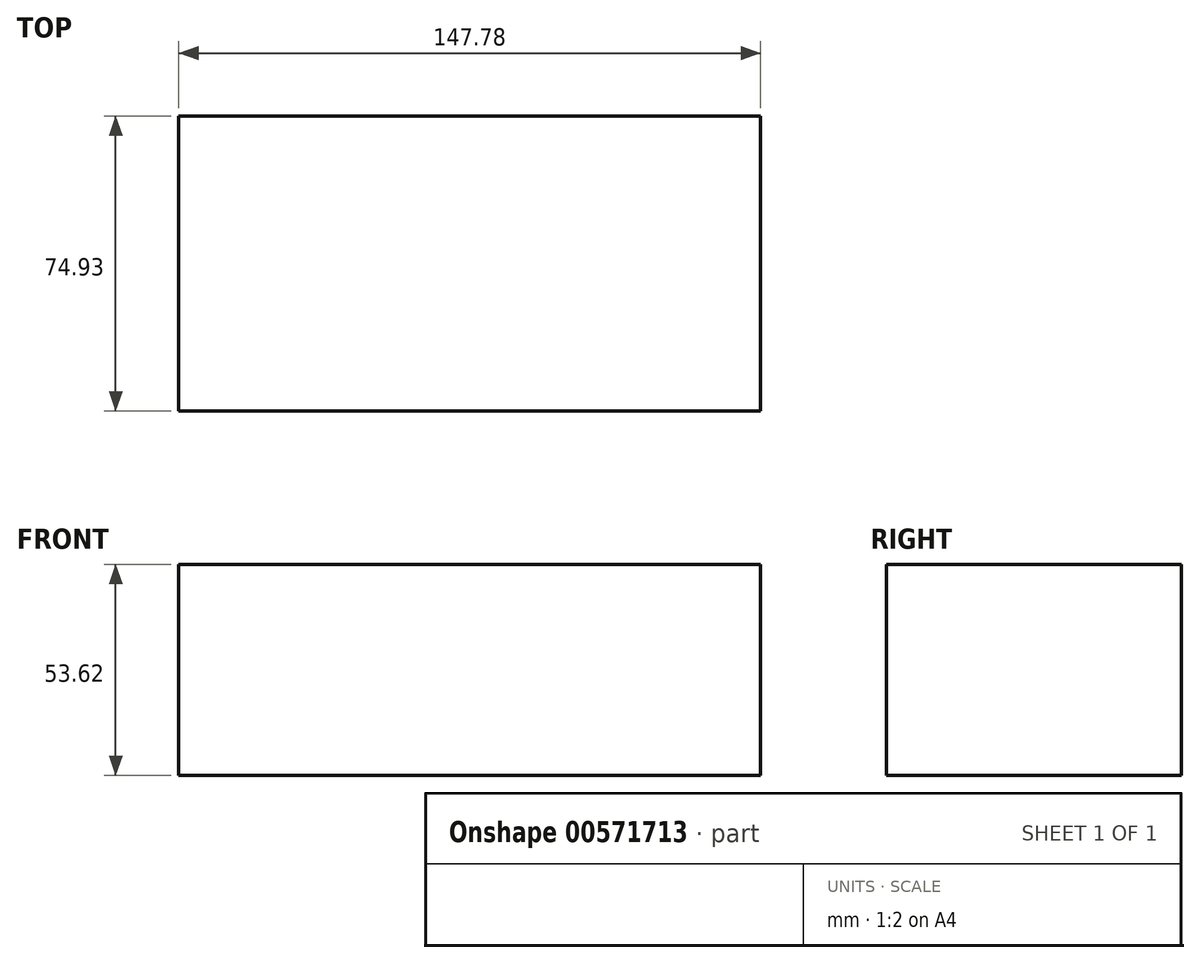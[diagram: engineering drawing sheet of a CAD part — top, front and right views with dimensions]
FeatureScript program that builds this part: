
annotation { "Feature Type Name" : "Feature", "Feature Type Description" : "" }
export const myFeature = defineFeature(function(context is Context, id is Id, definition is map)
    precondition{}
    {
        {
            var Q0;
            Q0=qCreatedBy(makeId("Front.planeOp"),FACE);
            var sketch = newSketch(context, id + "F0", { "sketchPlane" : qUnion([Q0])});
            skLineSegment(sketch, "E0.bottom", {"start": v(-67.36, 34.48) * mm, "end": v(80.42, 34.48) * mm});
            skLineSegment(sketch, "E0.top", {"start": v(-67.36, -19.14) * mm, "end": v(80.42, -19.14) * mm});
            skLineSegment(sketch, "E0.left", {"start": v(-67.36, 34.48) * mm, "end": v(-67.36, -19.14) * mm});
            skLineSegment(sketch, "E0.right", {"start": v(80.42, 34.48) * mm, "end": v(80.42, -19.14) * mm});
            skSolve(sketch);
        }
        {
            var Q0;
            Q0 = qSketchRegion(id + "F0", true);
            extrude(context, id + "F1", {"entities" : qUnion([Q0]), "depth" : 74.93 * mm, "offsetDistance" : 25.4 * mm});
        }
    });
